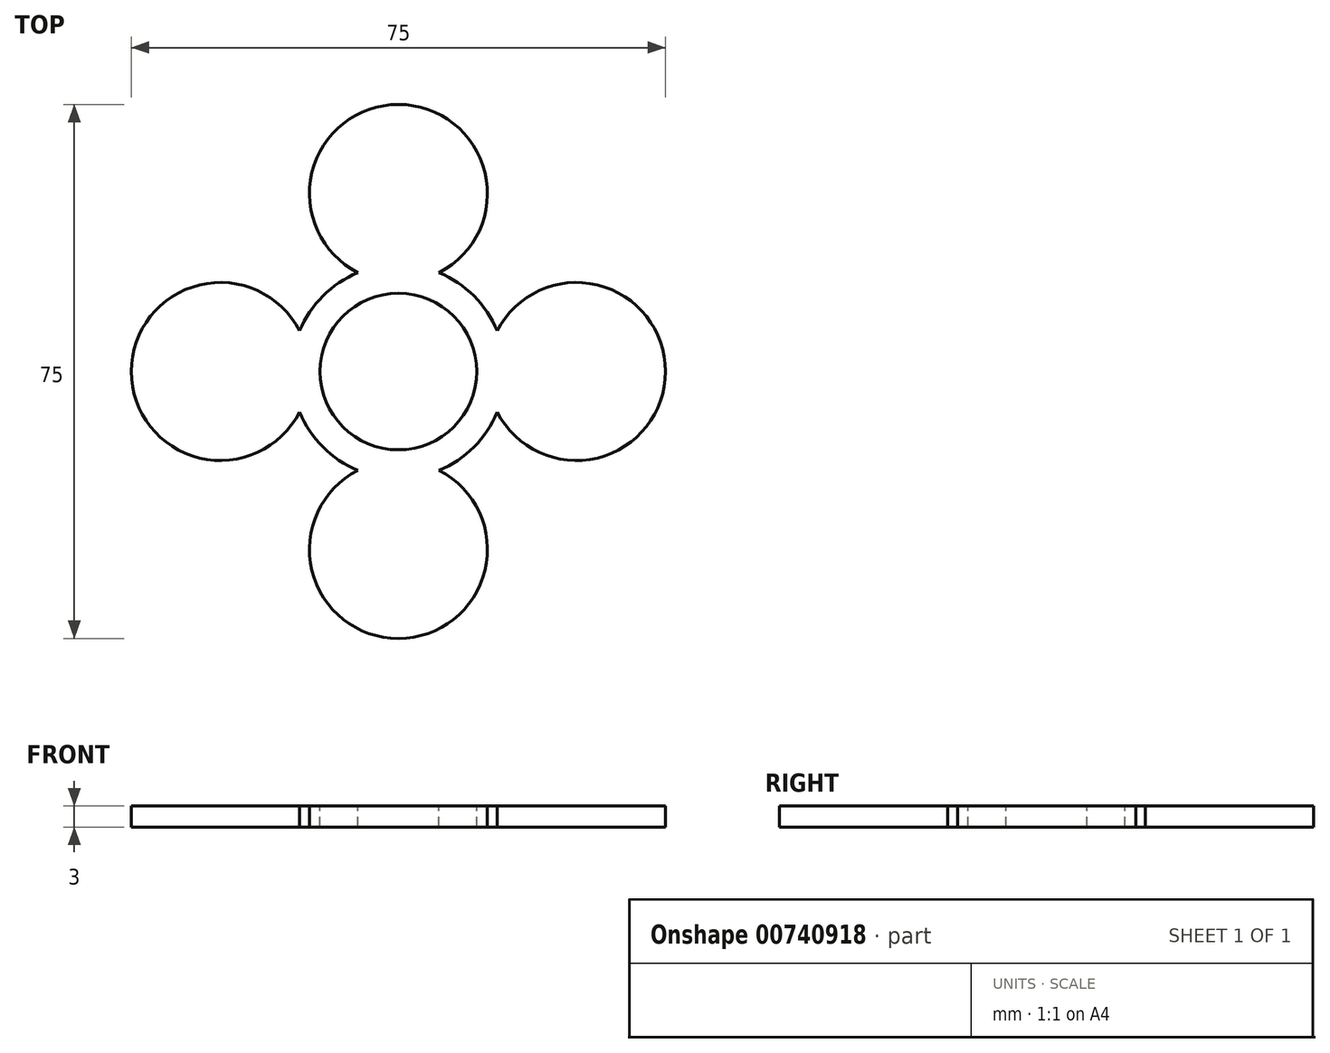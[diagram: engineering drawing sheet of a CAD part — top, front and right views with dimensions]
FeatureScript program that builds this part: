
annotation { "Feature Type Name" : "Feature", "Feature Type Description" : "" }
export const myFeature = defineFeature(function(context is Context, id is Id, definition is map)
    precondition{}
    {
        {
            var Q0;
            Q0=qCreatedBy(makeId("Top.planeOp"),FACE);
            var sketch = newSketch(context, id + "F0", { "sketchPlane" : qUnion([Q0])});
            skArc(sketch, "E0", {"start": v(7.78, 7.78) * mm, "mid": v(0, 11) * mm, "end": v(-7.78, 7.78) * mm});
            skArc(sketch, "E1", {"start": v(-5.7, 13.87) * mm, "mid": v(-8.32, 12.48) * mm, "end": v(-10.6, 10.6) * mm});
            skArc(sketch, "E2", {"start": v(5.7, 13.88) * mm, "mid": v(0, 37.5) * mm, "end": v(-5.7, 13.88) * mm});
            skArc(sketch, "E3.trimOffspring", {"start": v(10.6, 10.6) * mm, "mid": v(8.32, 12.48) * mm, "end": v(5.7, 13.88) * mm});
            skArc(sketch, "E4.1.0", {"start": v(-7.78, 7.78) * mm, "mid": v(-11, 0) * mm, "end": v(-7.78, -7.78) * mm});
            skArc(sketch, "E4.1.1", {"start": v(-10.6, 10.6) * mm, "mid": v(-12.48, 8.32) * mm, "end": v(-13.88, 5.7) * mm});
            skArc(sketch, "E4.1.2", {"start": v(-13.88, 5.7) * mm, "mid": v(-37.5, 0) * mm, "end": v(-13.88, -5.7) * mm});
            skArc(sketch, "E4.1.3", {"start": v(-13.87, -5.7) * mm, "mid": v(-12.48, -8.32) * mm, "end": v(-10.6, -10.6) * mm});
            skArc(sketch, "E4.2.0", {"start": v(-7.78, -7.78) * mm, "mid": v(0, -11) * mm, "end": v(7.78, -7.78) * mm});
            skArc(sketch, "E4.2.1", {"start": v(-10.6, -10.6) * mm, "mid": v(-8.32, -12.48) * mm, "end": v(-5.7, -13.87) * mm});
            skArc(sketch, "E4.2.2", {"start": v(-5.7, -13.88) * mm, "mid": v(0, -37.5) * mm, "end": v(5.7, -13.88) * mm});
            skArc(sketch, "E4.2.3", {"start": v(5.7, -13.87) * mm, "mid": v(8.32, -12.48) * mm, "end": v(10.6, -10.6) * mm});
            skArc(sketch, "E4.3.0", {"start": v(7.78, -7.78) * mm, "mid": v(11, 0) * mm, "end": v(7.78, 7.78) * mm});
            skArc(sketch, "E4.3.1", {"start": v(10.6, -10.6) * mm, "mid": v(12.48, -8.32) * mm, "end": v(13.87, -5.7) * mm});
            skArc(sketch, "E4.3.2", {"start": v(13.88, -5.7) * mm, "mid": v(37.5, 0) * mm, "end": v(13.88, 5.7) * mm});
            skArc(sketch, "E4.3.3", {"start": v(13.87, 5.7) * mm, "mid": v(12.48, 8.32) * mm, "end": v(10.6, 10.6) * mm});
            skSolve(sketch);
        }
        {
            var Q0;
            Q0 = qConstructionFilter(qBodyType(qCreatedBy(id + "F0" ,EDGE), BodyType.WIRE), ConstructionObject.NO);
            extrude(context, id + "F1", {"bodyType" : ToolBodyType.SURFACE, "surfaceEntities" : qUnion([Q0]), "depth" : 3 * mm, "offsetDistance" : 25 * mm});
        }
    });
